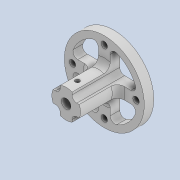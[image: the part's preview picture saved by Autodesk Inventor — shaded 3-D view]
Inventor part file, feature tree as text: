
AUTODESK INVENTOR PART (.ipt)
format: ipt  version: 2020 (Build 240168000, 168)  size: 260,608 bytes
history: native  units: mm
features: thicken_offset x4, other x4, extrude x3, sketch x3, projected_geometry x2, fillet x1, chamfer x1, reference x1
ambient origin geometry x8: Origin, YZ Plane, XZ Plane, XY Plane, X Axis, Y Axis, Z Axis, Center Point
bodies: Solid1 (feature_tree)
feature tree (19):
  extrude  "Extrusion1"  Depth=3.0mm TaperAngle=0.0deg
  extrude  "Extrusion2"  Depth=12.0mm TaperAngle=0.0deg
  fillet  "Fillet1"  Radius=2.0mm
  thicken_offset  "Thicken1"
  thicken_offset  "Thicken2"
  thicken_offset  "Thicken3"
  thicken_offset  "Thicken4"
  extrude  "Extrusion3"  Depth=1.0mm
  chamfer  "Chamfer1"  Distance=1.0mm
  sketch  "Sketch1"  dims[d0=3.0mm d1=3.0mm d2=0.0mm]
  reference  "Reference1"
  sketch  "Sketch2"  dims[d3=3.0mm d4=12.0mm d5=0.0mm d6=2.0mm]
  projected_geometry  "Projected Loop1"
  sketch  "Sketch3"  dims[d7=1.0mm d8=1.0mm d9=1.0mm d10=1.0mm d11=1.0mm d12=1.0mm d13=1.0mm d14=1.0mm d15=3.5mm d16=1.4mm d17=12.0mm d18=0.0mm d19=0.5mm d20=2.0mm d21=45.0deg]
  projected_geometry  "Projected Loop2"
  parser-record x1  (decoder bookkeeping rows leaked as tree rows — omitted from the tree; the rows remain in map.json)
  other  "tip_3_ass_base.iam"
  other  "mot_27_ass:1"
  other  "mot_27_1:1"
note: 1 file-system path scrubbed to <path> (originals preserved in map.json)
